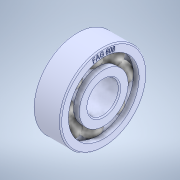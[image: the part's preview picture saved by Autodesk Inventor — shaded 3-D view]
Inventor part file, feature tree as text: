
AUTODESK INVENTOR PART (.ipt)
format: ipt  version: 2021.1 (Build 251245010, 245A)  size: 670,720 bytes
history: native  units: mm
features: other x8, fillet x1, revolve x1
ambient origin geometry x8: Origin, YZ Plane, XZ Plane, XY Plane, X Axis, Y Axis, Z Axis, Center Point
bodies: Solid1 (feature_tree), Solid2 (feature_tree), Solid3 (feature_tree), Solid4 (feature_tree), Solid5 (feature_tree), Solid6 (feature_tree), Solid7 (feature_tree), Solid8 (feature_tree), Solid9 (feature_tree), Solid10 (feature_tree)
feature tree (10):
  fillet  "Fillet2"  [1 undecoded]
  revolve  "Revolve2"  [1 undecoded]
  other  "CirPattern2[1]"
  other  "CirPattern2[2]"
  other  "CirPattern2[3]"
  other  "CirPattern2[4]"
  other  "CirPattern2[5]"
  other  "CirPattern2[6]"
  other  "CirPattern2[7]"
  other  "Cut-Extrude1"
note: 2 required parameter values undecoded (feature->parameter linkage not recoverable at this tier; creation-order binding heuristic only, values carry confidence <= 0.55)
